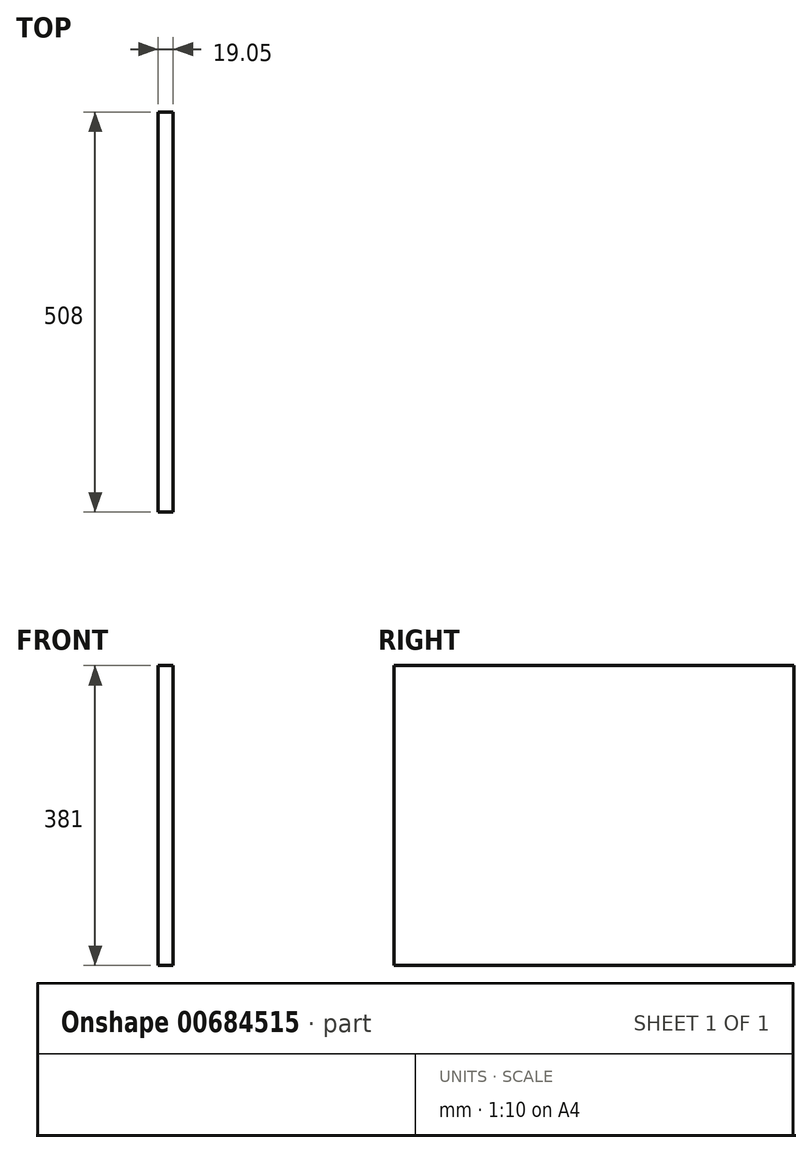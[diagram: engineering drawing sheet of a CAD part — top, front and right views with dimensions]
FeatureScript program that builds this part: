
annotation { "Feature Type Name" : "Feature", "Feature Type Description" : "" }
export const myFeature = defineFeature(function(context is Context, id is Id, definition is map)
    precondition{}
    {
        {
            var Q0;
            Q0=qCreatedBy(makeId("Right.planeOp"),FACE);
            var sketch = newSketch(context, id + "F0", { "sketchPlane" : qUnion([Q0])});
            skLineSegment(sketch, "E0.bottom", {"start": v(-345.4, 196.4) * mm, "end": v(162.6, 196.4) * mm});
            skLineSegment(sketch, "E0.top", {"start": v(-345.4, -184.6) * mm, "end": v(162.6, -184.6) * mm});
            skLineSegment(sketch, "E0.left", {"start": v(-345.4, 196.4) * mm, "end": v(-345.4, -184.6) * mm});
            skLineSegment(sketch, "E0.right", {"start": v(162.6, 196.4) * mm, "end": v(162.6, -184.6) * mm});
            skSolve(sketch);
        }
        {
            var Q0;
            Q0=makeQuery(id+"F0.imprint","IMPRINT",FACE,{"disambiguationData":[TD([[makeQuery(id+"F0.imprint","IMPRINT",EDGE,{"derivedFrom":sQuery(id+"F0.wireOp",EDGE,"E0.bottom")}),-1.0]])]});
            extrude(context, id + "F1", {"entities" : qUnion([Q0]), "depth" : 19.05 * mm, "offsetDistance" : 25.4 * mm});
        }
    });
